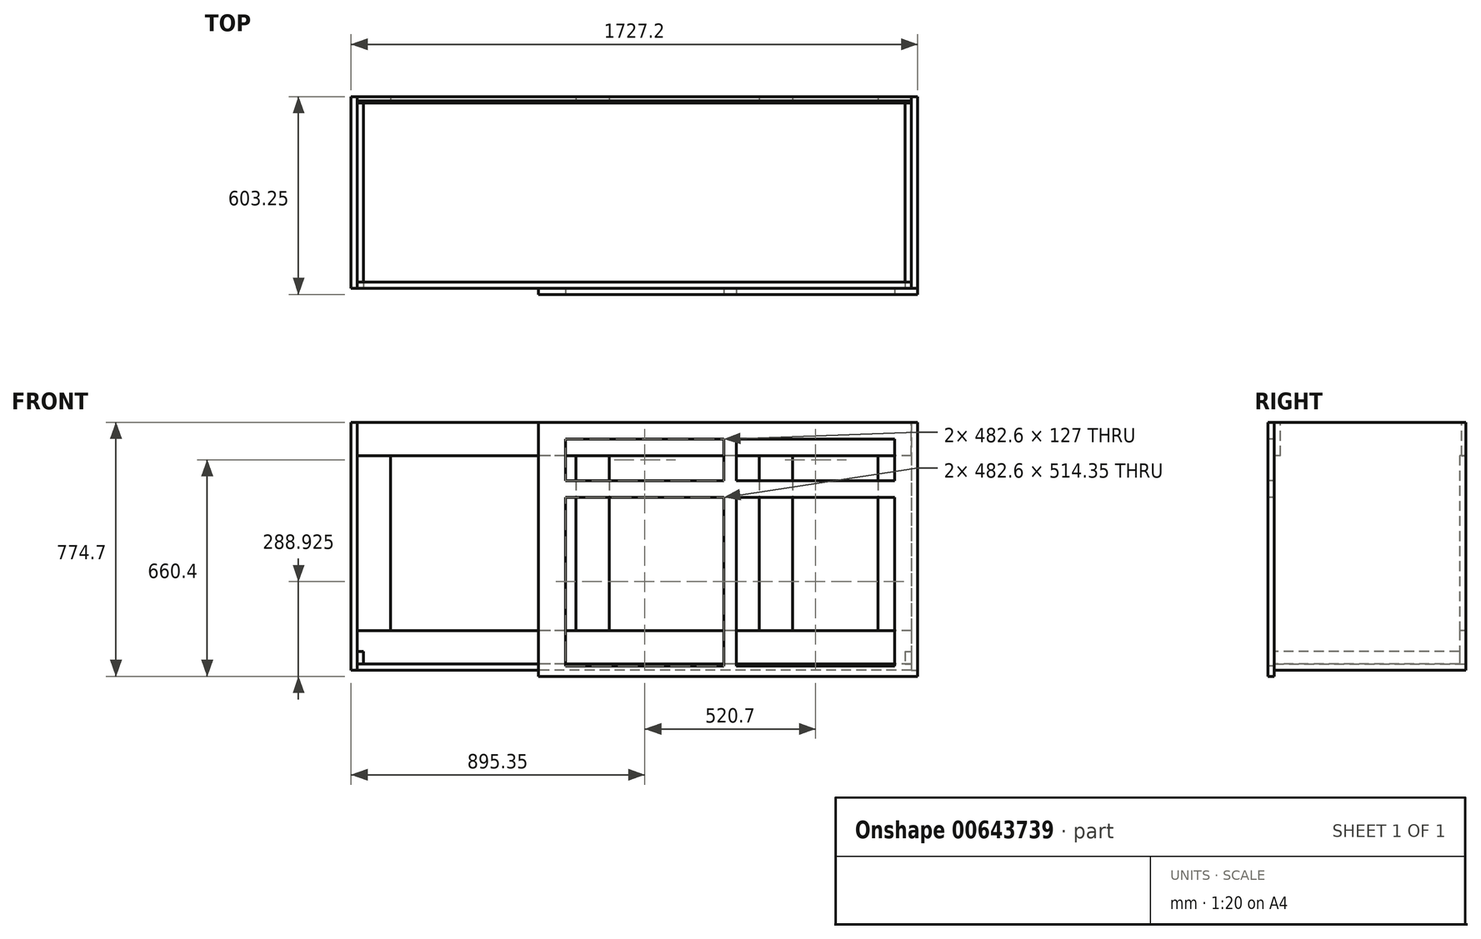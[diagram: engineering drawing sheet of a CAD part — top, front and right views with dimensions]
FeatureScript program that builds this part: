
annotation { "Feature Type Name" : "Feature", "Feature Type Description" : "" }
export const myFeature = defineFeature(function(context is Context, id is Id, definition is map)
    precondition{}
    {
        {
            var Q0;
            Q0=qCreatedBy(makeId("Top.planeOp"),FACE);
            var sketch = newSketch(context, id + "F0", { "sketchPlane" : qUnion([Q0])});
            skLineSegment(sketch, "E0.bottom", {"start": v(-844.55, -292.1) * mm, "end": v(-863.6, -292.1) * mm});
            skLineSegment(sketch, "E0.top", {"start": v(-844.55, 292.1) * mm, "end": v(-863.6, 292.1) * mm});
            skLineSegment(sketch, "E0.left", {"start": v(-844.55, -292.1) * mm, "end": v(-844.55, 292.1) * mm});
            skLineSegment(sketch, "E0.right", {"start": v(-863.6, -292.1) * mm, "end": v(-863.6, 292.1) * mm});
            skLineSegment(sketch, "E1.bottom", {"start": v(844.55, 292.1) * mm, "end": v(863.6, 292.1) * mm});
            skLineSegment(sketch, "E1.top", {"start": v(844.55, -292.1) * mm, "end": v(863.6, -292.1) * mm});
            skLineSegment(sketch, "E1.left", {"start": v(844.55, 292.1) * mm, "end": v(844.55, -292.1) * mm});
            skLineSegment(sketch, "E1.right", {"start": v(863.6, 292.1) * mm, "end": v(863.6, -292.1) * mm});
            skSolve(sketch);
        }
        {
            var Q0;
            Q0 = qSketchRegion(id + "F0", true);
            extrude(context, id + "F1", {"entities" : qUnion([Q0]), "depth" : 755.65 * mm, "offsetDistance" : 25.4 * mm});
        }
        {
            var Q0;
            Q0=makeQuery(id+"F1.opExtrude","SWEPT_FACE",FACE,{"disambiguationData":[OSD([sQuery(id+"F0.wireOp",EDGE,"E0.left")])]});
            var sketch = newSketch(context, id + "F2", { "sketchPlane" : qUnion([Q0])});
            skLineSegment(sketch, "E2.bottom", {"start": v(-292.1, 19.05) * mm, "end": v(292.1, 19.05) * mm});
            skLineSegment(sketch, "E2.top", {"start": v(-292.1, 0) * mm, "end": v(292.1, 0) * mm});
            skLineSegment(sketch, "E2.left", {"start": v(-292.1, 19.05) * mm, "end": v(-292.1, 0) * mm});
            skLineSegment(sketch, "E2.right", {"start": v(292.1, 19.05) * mm, "end": v(292.1, 0) * mm});
            skSolve(sketch);
        }
        {
            var Q0;
            Q0 = qSketchRegion(id + "F2", true);
            extrude(context, id + "F3", {"entities" : qUnion([Q0]), "depth" : 1689.1 * mm, "offsetDistance" : 25.4 * mm});
        }
        {
            var Q0;
            Q0=makeQuery(id+"F1.opExtrude","SWEPT_FACE",FACE,{"disambiguationData":[OSD([sQuery(id+"F0.wireOp",EDGE,"E0.bottom")])]});
            var sketch = newSketch(context, id + "F4", { "sketchPlane" : qUnion([Q0])});
            skLineSegment(sketch, "E3.bottom", {"start": v(-844.55, 57.15) * mm, "end": v(-825.5, 57.15) * mm});
            skLineSegment(sketch, "E3.top", {"start": v(-844.55, 19.05) * mm, "end": v(-825.5, 19.05) * mm});
            skLineSegment(sketch, "E3.left", {"start": v(-844.55, 57.15) * mm, "end": v(-844.55, 19.05) * mm});
            skLineSegment(sketch, "E3.right", {"start": v(-825.5, 57.15) * mm, "end": v(-825.5, 19.05) * mm});
            skLineSegment(sketch, "E4.bottom", {"start": v(825.5, 57.15) * mm, "end": v(844.55, 57.15) * mm});
            skLineSegment(sketch, "E4.top", {"start": v(825.5, 19.05) * mm, "end": v(844.55, 19.05) * mm});
            skLineSegment(sketch, "E4.left", {"start": v(825.5, 57.15) * mm, "end": v(825.5, 19.05) * mm});
            skLineSegment(sketch, "E4.right", {"start": v(844.55, 57.15) * mm, "end": v(844.55, 19.05) * mm});
            skSolve(sketch);
        }
        {
            var Q0;
            Q0 = qSketchRegion(id + "F4", true);
            extrude(context, id + "F5", {"entities" : qUnion([Q0]), "depth" : -565.15 * mm, "offsetDistance" : 25.4 * mm});
        }
        {
            var Q0;
            Q0=makeQuery(id+"F1.opExtrude","SWEPT_FACE",FACE,{"disambiguationData":[OSD([sQuery(id+"F0.wireOp",EDGE,"E0.left")])]});
            var sketch = newSketch(context, id + "F6", { "sketchPlane" : qUnion([Q0])});
            skLineSegment(sketch, "E5.bottom", {"start": v(-273.05, 654.05) * mm, "end": v(-292.1, 654.05) * mm});
            skLineSegment(sketch, "E5.top", {"start": v(-273.05, 755.65) * mm, "end": v(-292.1, 755.65) * mm});
            skLineSegment(sketch, "E5.left", {"start": v(-273.05, 654.05) * mm, "end": v(-273.05, 755.65) * mm});
            skLineSegment(sketch, "E5.right", {"start": v(-292.1, 654.05) * mm, "end": v(-292.1, 755.65) * mm});
            skLineSegment(sketch, "E6.bottom", {"start": v(279.4, 654.05) * mm, "end": v(292.1, 654.05) * mm});
            skLineSegment(sketch, "E6.top", {"start": v(279.4, 755.65) * mm, "end": v(292.1, 755.65) * mm});
            skLineSegment(sketch, "E6.left", {"start": v(279.4, 654.05) * mm, "end": v(279.4, 755.65) * mm});
            skLineSegment(sketch, "E6.right", {"start": v(292.1, 654.05) * mm, "end": v(292.1, 755.65) * mm});
            skLineSegment(sketch, "E7.bottom", {"start": v(273.05, 120.65) * mm, "end": v(292.1, 120.65) * mm});
            skLineSegment(sketch, "E7.top", {"start": v(273.05, 19.05) * mm, "end": v(292.1, 19.05) * mm});
            skLineSegment(sketch, "E7.left", {"start": v(273.05, 120.65) * mm, "end": v(273.05, 19.05) * mm});
            skLineSegment(sketch, "E7.right", {"start": v(292.1, 120.65) * mm, "end": v(292.1, 19.05) * mm});
            skSolve(sketch);
        }
        {
            var Q0;
            Q0 = qSketchRegion(id + "F6", true);
            extrude(context, id + "F7", {"entities" : qUnion([Q0]), "depth" : 1689.1 * mm, "offsetDistance" : 25.4 * mm});
        }
        {
            var Q0;
            Q0=makeQuery(id+"F7.opExtrude","SWEPT_FACE",FACE,{"disambiguationData":[OSD([sQuery(id+"F6.wireOp",EDGE,"E7.bottom")])]});
            var sketch = newSketch(context, id + "F8", { "sketchPlane" : qUnion([Q0])});
            skLineSegment(sketch, "E8.bottom", {"start": v(-844.55, 292.1) * mm, "end": v(-742.95, 292.1) * mm});
            skLineSegment(sketch, "E8.top", {"start": v(-844.55, 273.05) * mm, "end": v(-742.95, 273.05) * mm});
            skLineSegment(sketch, "E8.left", {"start": v(-844.55, 292.1) * mm, "end": v(-844.55, 273.05) * mm});
            skLineSegment(sketch, "E8.right", {"start": v(-742.95, 292.1) * mm, "end": v(-742.95, 273.05) * mm});
            skLineSegment(sketch, "E9.bottom", {"start": v(381, 292.1) * mm, "end": v(482.6, 292.1) * mm});
            skLineSegment(sketch, "E9.top", {"start": v(381, 273.05) * mm, "end": v(482.6, 273.05) * mm});
            skLineSegment(sketch, "E9.left", {"start": v(381, 292.1) * mm, "end": v(381, 273.05) * mm});
            skLineSegment(sketch, "E9.right", {"start": v(482.6, 292.1) * mm, "end": v(482.6, 273.05) * mm});
            skLineSegment(sketch, "E10.bottom", {"start": v(-177.8, 292.1) * mm, "end": v(-76.2, 292.1) * mm});
            skLineSegment(sketch, "E10.top", {"start": v(-177.8, 273.05) * mm, "end": v(-76.2, 273.05) * mm});
            skLineSegment(sketch, "E10.left", {"start": v(-177.8, 292.1) * mm, "end": v(-177.8, 273.05) * mm});
            skLineSegment(sketch, "E10.right", {"start": v(-76.2, 292.1) * mm, "end": v(-76.2, 273.05) * mm});
            skLineSegment(sketch, "E11.bottom", {"start": v(742.95, 292.1) * mm, "end": v(844.55, 292.1) * mm});
            skLineSegment(sketch, "E11.top", {"start": v(742.95, 273.05) * mm, "end": v(844.55, 273.05) * mm});
            skLineSegment(sketch, "E11.left", {"start": v(742.95, 292.1) * mm, "end": v(742.95, 273.05) * mm});
            skLineSegment(sketch, "E11.right", {"start": v(844.55, 292.1) * mm, "end": v(844.55, 273.05) * mm});
            skSolve(sketch);
        }
        {
            var Q0;
            Q0 = qSketchRegion(id + "F8", true);
            extrude(context, id + "F9", {"entities" : qUnion([Q0]), "depth" : 533.4 * mm, "offsetDistance" : 25.4 * mm});
        }
        {
            var Q0;
            Q0=makeQuery(id+"F7.opExtrude","SWEPT_FACE",FACE,{"disambiguationData":[OSD([sQuery(id+"F6.wireOp",EDGE,"E5.right")])]});
            var sketch = newSketch(context, id + "F10", { "sketchPlane" : qUnion([Q0])});
            skLineSegment(sketch, "E12.bottom", {"start": v(-292.1, 755.65) * mm, "end": v(863.6, 755.65) * mm});
            skLineSegment(sketch, "E12.top", {"start": v(-292.1, -19.05) * mm, "end": v(863.6, -19.05) * mm});
            skLineSegment(sketch, "E12.left", {"start": v(-292.1, 755.65) * mm, "end": v(-292.1, -19.05) * mm});
            skLineSegment(sketch, "E12.right", {"start": v(863.6, 755.65) * mm, "end": v(863.6, -19.05) * mm});
            skSolve(sketch);
        }
        {
            var Q0;
            Q0 = qSketchRegion(id + "F10", true);
            extrude(context, id + "F11", {"entities" : qUnion([Q0]), "depth" : 19.05 * mm, "offsetDistance" : 25.4 * mm});
        }
        {
            var Q0;
            Q0=makeQuery(id+"F11.opExtrude","CAP_FACE",FACE,{"disambiguationData":[OSD([sQuery(id+"F10.wireOp",EDGE,"E12.bottom"),sQuery(id+"F10.wireOp",EDGE,"E12.top"),sQuery(id+"F10.wireOp",EDGE,"E12.left"),sQuery(id+"F10.wireOp",EDGE,"E12.right")])],"isStart":false});
            var sketch = newSketch(context, id + "F12", { "sketchPlane" : qUnion([Q0])});
            skLineSegment(sketch, "E13.bottom", {"start": v(311.15, 704.85) * mm, "end": v(793.75, 704.85) * mm});
            skLineSegment(sketch, "E13.top", {"start": v(311.15, 577.85) * mm, "end": v(793.75, 577.85) * mm});
            skLineSegment(sketch, "E13.left", {"start": v(311.15, 704.85) * mm, "end": v(311.15, 577.85) * mm});
            skLineSegment(sketch, "E13.right", {"start": v(793.75, 704.85) * mm, "end": v(793.75, 577.85) * mm});
            skLineSegment(sketch, "E14.bottom", {"start": v(-209.55, 527.05) * mm, "end": v(273.05, 527.05) * mm});
            skLineSegment(sketch, "E14.top", {"start": v(-209.55, 12.7) * mm, "end": v(273.05, 12.7) * mm});
            skLineSegment(sketch, "E14.left", {"start": v(-209.55, 527.05) * mm, "end": v(-209.55, 12.7) * mm});
            skLineSegment(sketch, "E14.right", {"start": v(273.05, 527.05) * mm, "end": v(273.05, 12.7) * mm});
            skLineSegment(sketch, "E15.bottom", {"start": v(311.15, 527.05) * mm, "end": v(793.75, 527.05) * mm});
            skLineSegment(sketch, "E15.top", {"start": v(311.15, 12.7) * mm, "end": v(793.75, 12.7) * mm});
            skLineSegment(sketch, "E15.left", {"start": v(311.15, 527.05) * mm, "end": v(311.15, 12.7) * mm});
            skLineSegment(sketch, "E15.right", {"start": v(793.75, 527.05) * mm, "end": v(793.75, 12.7) * mm});
            skLineSegment(sketch, "E16.bottom", {"start": v(-209.55, 704.85) * mm, "end": v(273.05, 704.85) * mm});
            skLineSegment(sketch, "E16.top", {"start": v(-209.55, 577.85) * mm, "end": v(273.05, 577.85) * mm});
            skLineSegment(sketch, "E16.left", {"start": v(-209.55, 704.85) * mm, "end": v(-209.55, 577.85) * mm});
            skLineSegment(sketch, "E16.right", {"start": v(273.05, 704.85) * mm, "end": v(273.05, 577.85) * mm});
            skSolve(sketch);
        }
        {
            var Q0;
            Q0 = qSketchRegion(id + "F12", true);
            extrude(context, id + "F13", {"entities" : qUnion([Q0]), "operationType" : NewBodyOperationType.REMOVE, "oppositeDirection" : true, "depth" : 19.05 * mm, "offsetDistance" : 25.4 * mm});
        }
    });
